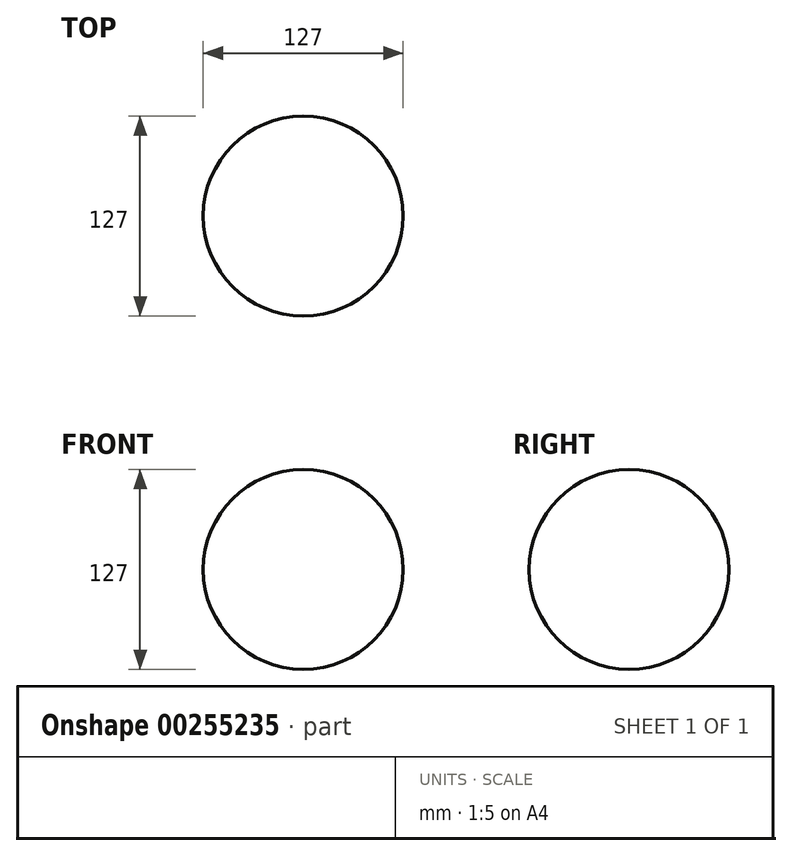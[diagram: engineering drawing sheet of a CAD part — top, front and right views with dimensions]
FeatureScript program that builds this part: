
annotation { "Feature Type Name" : "Feature", "Feature Type Description" : "" }
export const myFeature = defineFeature(function(context is Context, id is Id, definition is map)
    precondition{}
    {
        {
            var Q0;
            Q0=qCreatedBy(makeId("Front.planeOp"),FACE);
            var sketch = newSketch(context, id + "F0", { "sketchPlane" : qUnion([Q0])});
            skCircle(sketch, "E0", {"center": v(0, 0) * mm, "radius": 63.5 * mm});
            skSolve(sketch);
        }
        {
            var Q0;
            Q0=makeQuery(id+"F0.imprint","IMPRINT",FACE,{"disambiguationData":[TD([[makeQuery(id+"F0.imprint","IMPRINT",EDGE,{"derivedFrom":sQuery(id+"F0.wireOp",EDGE,"E0")}),1.0]])]});
            extrude(context, id + "F1", {"entities" : qUnion([Q0]), "endBound" : BoundingType.SYMMETRIC, "depth" : 127 * mm});
        }
        {
            var Q0;
            Q0=makeQuery(id+"F1.opExtrude","SWEPT_FACE",FACE,{"disambiguationData":[OSD([sQuery(id+"F0.wireOp",EDGE,"E0")])]});
            fillet(context, id + "F2", {"entities" : qUnion([Q0]), "radius" : 63.5 * mm, "tangentPropagation" : true, "allowEdgeOverflow" : false});
        }
    });
